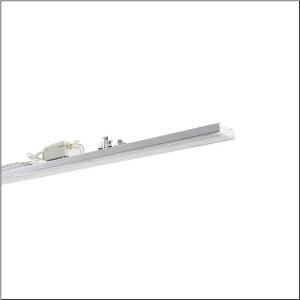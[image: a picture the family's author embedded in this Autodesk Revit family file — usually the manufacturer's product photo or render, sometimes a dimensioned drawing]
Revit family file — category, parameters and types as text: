
# Revit family: licross_11_recessed_mo_51tl18dv4e5g
name_source: partatom
category: Lighting Fixtures
units: mm (PartAtom-declared; Revit-internal decimal feet)

## family parameters
Cut with Voids When Loaded = No
Host = Face
Light Source = No
Part Type = Normal
Room Calculation Point = No
Round Connector Dimension = Use Diameter
Shared = No

## types (1)
- --- (1 x LED, 14920 lm, 84.1 W, 4000K)
    Apparent Load = 84 VA
    CIE Flux Codes = 83 96 99 100 100
    Color Rendering = 80
    Color Temperature = 4000K
    Default Elevation = 1800 mm
    Description = Licross 11 Recessed MO, luminaire insert, of sheet steel, coil coated, white, length: 2.250mm, width: 66mm, height: 67mm, LED rated luminous flux: 14.920lm, light colour: 840, SDCM (Standard Deviation of Colour Matching)MacAdam ≤ 2 SDCM (initial), control gear: DALI 2, with plug, 5-pole, with phase selection, mains connection: 220..240V, AC, 50/60Hz, rated input power: 84W, internal wiring halogen-free, primary light control with lens, of plastic, primary optical cover: cover, of PMMA, light emission: direct distribution, primary light characteristic: symmetric, protection rating (complete): IP40, insulation class (complete): insulation class I (protective earthing), certification: CE, ENEC, VDE, UKCA, protection symbol: D if used in an environment without relevant dust loads with corresponding accessories, impact resistance: IK06, permissible ambient temperature for indoor applications: -25..+35°C, corresponds to IFS (International Featured Standards) requirements for safety and quality in the food industry, reducing of maximum allowable ambient temperature of 5°C with ceiling mounting, LABS conformity tested according to VDMA 24364:2018-05, The light source and the operating device comply with the requirements of the Ecodesign Regulation (EU) 2019/2020 and are replaceable in accordance with this regulation, packaging unit: 1 piece
    Height = 58 mm
    Lamp = 1 x LED
    Lamp Light Flux = 14920 lm
    Lamp Power = 84.1 W
    Lamp count = 1
    Length = 2250 mm
    Luminous efficacy = 177 lm/W
    Manufacturer = Siteco
    ModVariant = No
    Model = 51TL18DV4E5G
    Mounting Place = Ceiling
    Mounting Type = Pendant
    Number of Poles = 1
    OnlyDefault = Yes
    Power Factor = 1
    Product Name = Licross 11 Recessed MO
    Product group = luminaire insert | ceiling pendant
    ProductGroupID = 901
    Protection Class = Protection class I
    Protection Degree = IP 40
    RLX_Detail_Level = 1
    RLX_Emergency_Light_Flux = 0 lm
    RLX_Emergency_Type = 0
    RLX_Emergency_Type_DB = No
    RlxData = <blob elided: 29545 chars, md5=48c40dff>
    Socket = socket
    Standby Power = 0 W
    System Light Flux = 14920 lm
    System Power = 84 W
    Type Comments = factory setting: luminous flux: 100 % | dim-lin: 254 | 378 mA
    Type Image = l_1296930.jpg
    URL = http://relux.com
    VarID = @adj_102209
    Voltage = 0 V
    Weight = 0.00 kg
    Width = 66 mm

## geometry (parser evidence)
native form markers: Blend x4, Sweep x9
no freeform markers — native parametric forms only
